# Revit family: Climaver_Connection to a grille or diffuser
name_source: partatom
category: Tvarovky potrubí
units: mm (PartAtom-declared; Revit-internal decimal feet)

## family parameters
Kóta kulaté spojky = Použít průměr
Nadpis OmniClass = Air Ductwork
Ořezat dutým tvarem při načtení = Ne
Sdílené = Ne
Typ dílu = Vývod – nastavitelný
Vždy vertikální = Ano
Založené na pracovní rovině = Ne
Číslo OmniClass = 23.75.70.14

## types (2) — shared parameters
COUNT = 1
Komentáře k typům = Glass wool duct boards for air conditioning, ventilation and heating systems. The system allow to make foursquare duct/duct lines (straight duct, elbow, offset, branch etc.) The panel a high density glass wool duct board and is faced on both sides. The outer facing, a robust aluminum facing, acts as a vapor barrier and ensures that the duct is airtight. The inner facing of the duct may be either a reinforced aluminum facing or a woven glass facing.The pre-insulated, self-supporting duct is designed to offer excellent acoustics, excellent thermal performance and a high level of air-tightness, making the system energy efficient. Application as EN 13403, Airtightness: Thermal conductivity λ = 0,032 [W/(m·K)] for T = 10 °C, Class D, Maximum Static pressure: 800 Pa, Maximum air speed: 18 m/s, Maximum temperature of circulating air: 90°C, Maximum external air temperature 60°C, Minimum temperature: – 30˚C, Dimensional stability: Quantities and measured values : <1 %, Duct assembly: exclusive male/female molded shiplap, Water-vapour diffusion resistence: >140 m².h.Pa/mg (from the facing).
Material = <Podle kategorie>
Model = connection to a grille of diffuser
Popis = Connection to a grille or diffuser
TYPE = Fitting
URL = https://www.isover-technical-insulation.com
Výrobce = Saint-Gobain - Isover
Warnings = Ano
zero-valued in all types: Výchozí výška

## per-type parameters (varying)
| type | Délka odbočení | Family collaps | PANEL THICKNESS |
| 25mm | 25.0000 mm | Ne | 25 mm  [stored 0.082021 ft] |
| 40mm | 50.0000 mm | Ano | 40 mm  [stored 0.131234 ft] |

note: [stored X ft] marks values corroborated as IEEE doubles in the binary element streams (Revit-internal decimal feet)

## geometry (parser evidence)
native form markers: Sweep x3
no freeform markers — native parametric forms only
